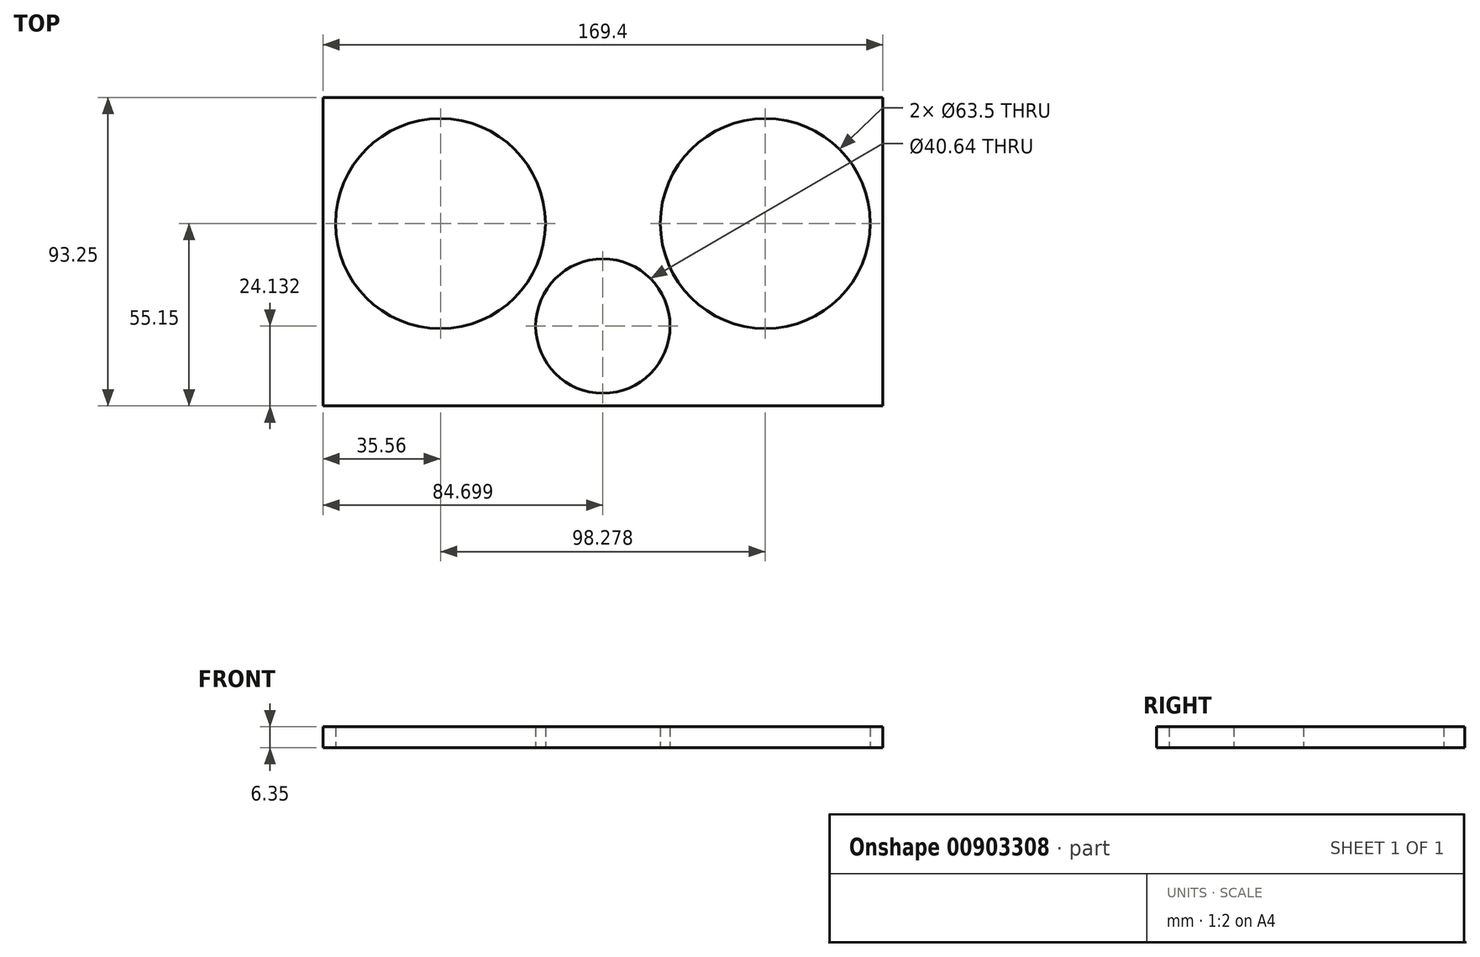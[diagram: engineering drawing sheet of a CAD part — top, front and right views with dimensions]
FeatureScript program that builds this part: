
annotation { "Feature Type Name" : "Feature", "Feature Type Description" : "" }
export const myFeature = defineFeature(function(context is Context, id is Id, definition is map)
    precondition{}
    {
        {
            var Q0;
            Q0=qCreatedBy(makeId("Top.planeOp"),FACE);
            var sketch = newSketch(context, id + "F0", { "sketchPlane" : qUnion([Q0])});
            skLineSegment(sketch, "E0.bottom", {"start": v(0, 0) * mm, "end": v(169.4, 0) * mm});
            skLineSegment(sketch, "E0.top", {"start": v(0, -93.25) * mm, "end": v(169.4, -93.25) * mm});
            skLineSegment(sketch, "E0.left", {"start": v(0, 0) * mm, "end": v(0, -93.25) * mm});
            skLineSegment(sketch, "E0.right", {"start": v(169.4, 0) * mm, "end": v(169.4, -93.25) * mm});
            skCircle(sketch, "E1", {"center": v(35.56, -38.1) * mm, "radius": 31.75 * mm});
            skCircle(sketch, "E2", {"center": v(133.84, -38.1) * mm, "radius": 31.75 * mm});
            skCircle(sketch, "E3", {"center": v(84.7, -69.12) * mm, "radius": 20.32 * mm});
            skPoint(sketch, "E3.centerSnap0", {"position": v(84.7, 0) * mm});
            skLineSegment(sketch, "E4", {"start": v(0, -38.1) * mm, "end": v(35.56, -38.1) * mm, "construction": true});
            skSolve(sketch);
        }
        {
            var Q0;
            Q0=makeQuery(id+"F0.imprint","IMPRINT",FACE,{"disambiguationData":[TD([[makeQuery(id+"F0.imprint","IMPRINT",EDGE,{"derivedFrom":sQuery(id+"F0.wireOp",EDGE,"E0.bottom")}),-1.0]])]});
            extrude(context, id + "F1", {"entities" : qUnion([Q0]), "depth" : 6.35 * mm, "offsetDistance" : 25.4 * mm});
        }
    });
